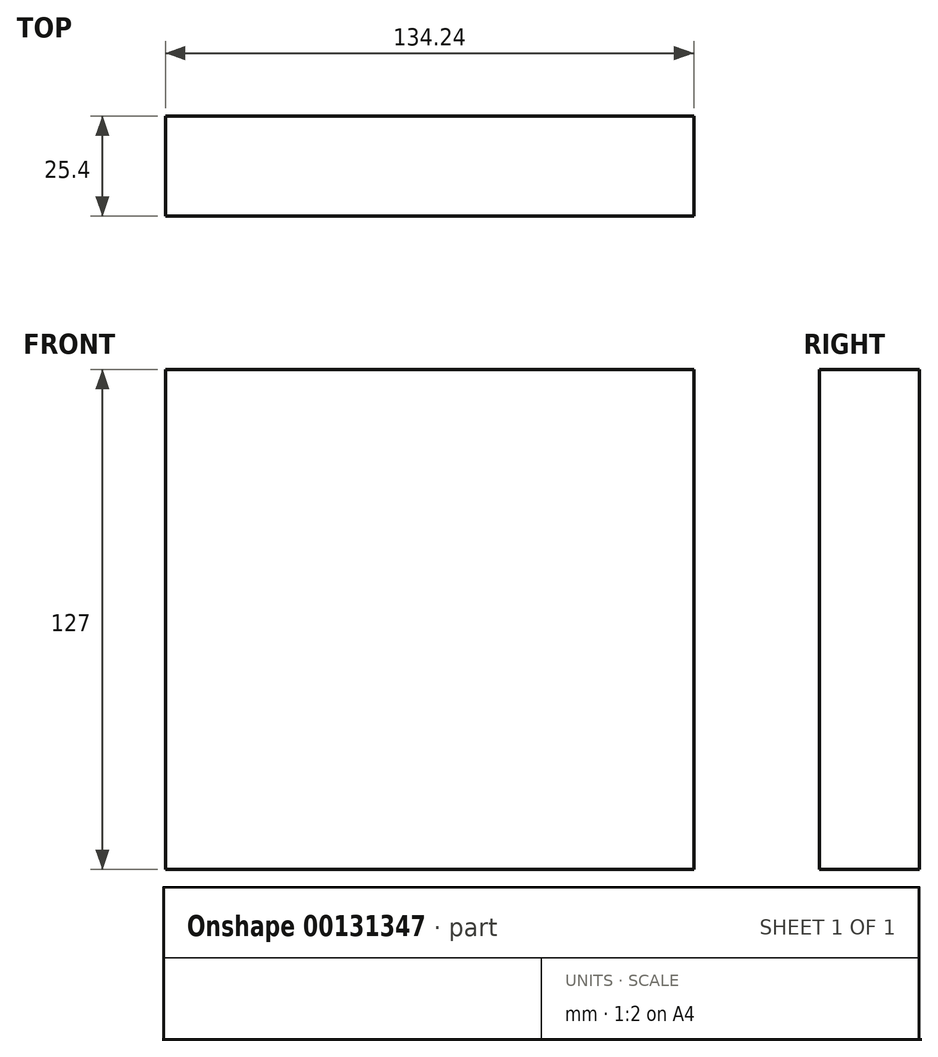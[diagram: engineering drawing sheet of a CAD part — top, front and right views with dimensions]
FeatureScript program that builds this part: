
annotation { "Feature Type Name" : "Feature", "Feature Type Description" : "" }
export const myFeature = defineFeature(function(context is Context, id is Id, definition is map)
    precondition{}
    {
        {
            var Q0;
            Q0=qCreatedBy(makeId("Front.planeOp"),FACE);
            var sketch = newSketch(context, id + "F0", { "sketchPlane" : qUnion([Q0])});
            skLineSegment(sketch, "E0.bottom", {"start": v(67.12, -63.5) * mm, "end": v(-67.12, -63.5) * mm});
            skLineSegment(sketch, "E0.top", {"start": v(67.12, 63.5) * mm, "end": v(-67.12, 63.5) * mm});
            skLineSegment(sketch, "E0.left", {"start": v(67.12, -63.5) * mm, "end": v(67.12, 63.5) * mm});
            skLineSegment(sketch, "E0.right", {"start": v(-67.12, -63.5) * mm, "end": v(-67.12, 63.5) * mm});
            skPoint(sketch, "E0.middle", {"position": v(0, 0) * mm});
            skSolve(sketch);
        }
        {
            var Q0;
            Q0 = qSketchRegion(id + "F0", true);
            extrude(context, id + "F1", {"entities" : qUnion([Q0]), "depth" : 25.4 * mm});
        }
    });
